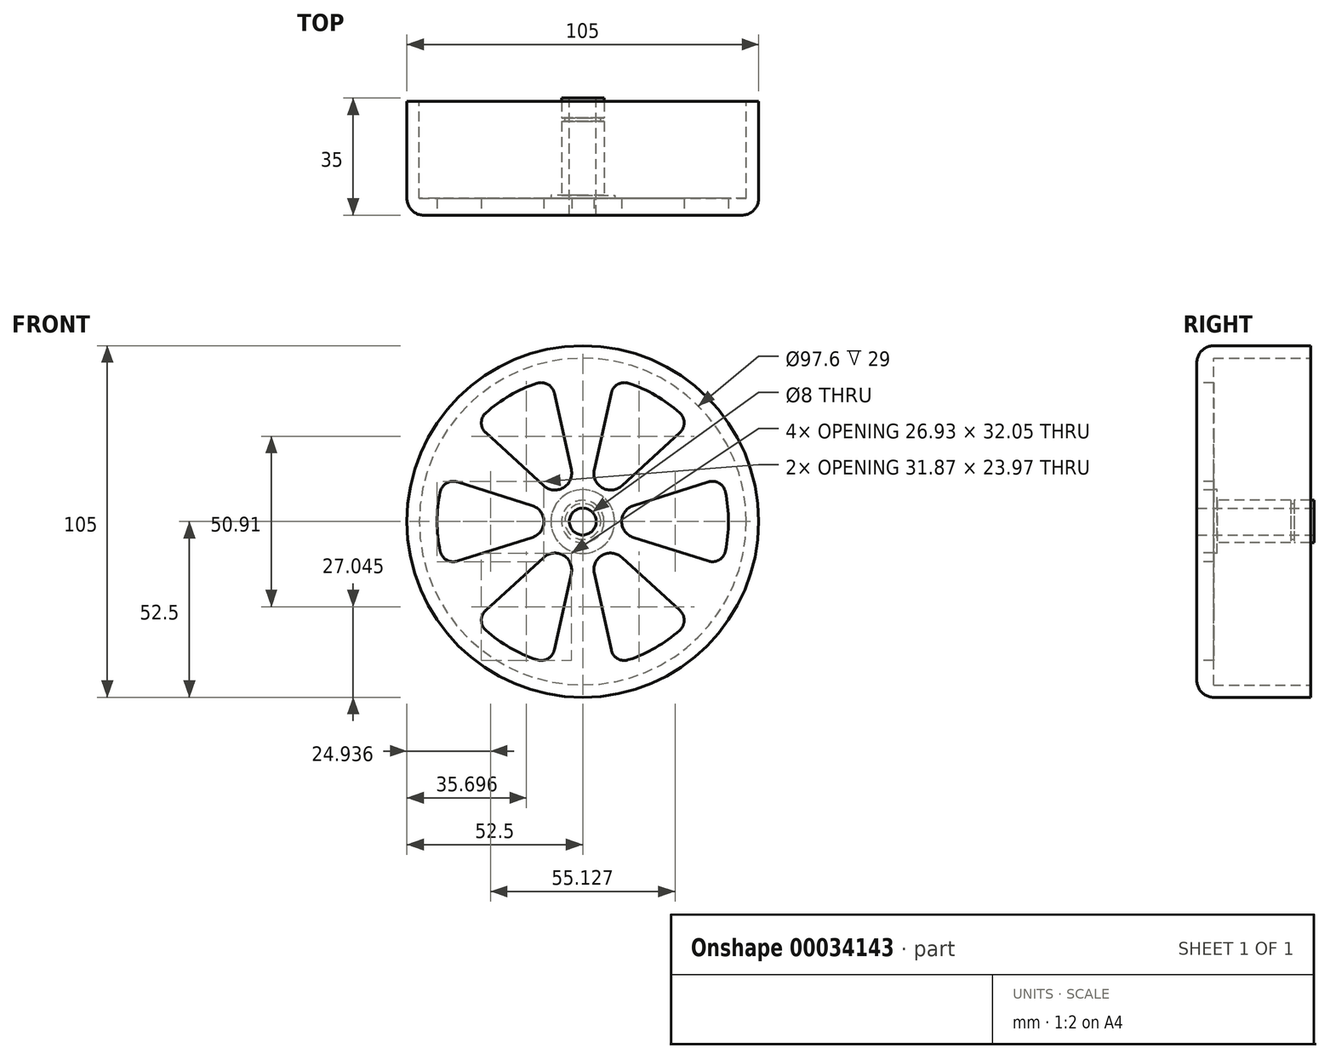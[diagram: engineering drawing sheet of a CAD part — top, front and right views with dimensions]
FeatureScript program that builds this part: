
annotation { "Feature Type Name" : "Feature", "Feature Type Description" : "" }
export const myFeature = defineFeature(function(context is Context, id is Id, definition is map)
    precondition{}
    {
        {
            var Q0;
            Q0=qCreatedBy(makeId("Front.planeOp"),FACE);
            var sketch = newSketch(context, id + "F0", { "sketchPlane" : qUnion([Q0])});
            skCircle(sketch, "E0", {"center": v(0, 0) * mm, "radius": 48.8 * mm});
            skCircle(sketch, "E1", {"center": v(0, 0) * mm, "radius": 52.5 * mm});
            skSolve(sketch);
        }
        {
            var Q0;
            Q0 = qSketchRegion(id + "F0", true);
            extrude(context, id + "F1", {"entities" : qUnion([Q0]), "depth" : 29 * mm});
        }
        {
            var Q0;
            Q0=makeQuery(id+"F1.opExtrude","CAP_FACE",FACE,{"disambiguationData":[OSD([sQuery(id+"F0.wireOp",EDGE,"E0"),sQuery(id+"F0.wireOp",EDGE,"E1")])],"isStart":false});
            var sketch = newSketch(context, id + "F2", { "sketchPlane" : qUnion([Q0])});
            skCircle(sketch, "E2.0", {"center": v(0, 0) * mm, "radius": 52.5 * mm});
            skCircle(sketch, "E3", {"center": v(0, 0) * mm, "radius": 4 * mm});
            skSolve(sketch);
        }
        {
            var Q0;
            Q0 = qSketchRegion(id + "F2", true);
            extrude(context, id + "F3", {"entities" : qUnion([Q0]), "operationType" : NewBodyOperationType.ADD, "depth" : 5 * mm});
        }
        {
            var Q0;
            Q0=makeQuery(id+"F3.opExtrude","CAP_FACE",FACE,{"disambiguationData":[OSD([sQuery(id+"F2.wireOp",EDGE,"E2.0"),sQuery(id+"F2.wireOp",EDGE,"E3")])],"isStart":true});
            var sketch = newSketch(context, id + "F4", { "sketchPlane" : qUnion([Q0])});
            skCircle(sketch, "E4", {"center": v(0, 0) * mm, "radius": 6.35 * mm});
            skCircle(sketch, "E5.0", {"center": v(0, 0) * mm, "radius": 4 * mm});
            skSolve(sketch);
        }
        {
            var Q0;
            Q0 = qSketchRegion(id + "F4", true);
            extrude(context, id + "F5", {"entities" : qUnion([Q0]), "operationType" : NewBodyOperationType.ADD, "depth" : 30 * mm});
        }
        {
            var Q0;
            Q0=makeQuery(id+"F5.opExtrude","CAP_FACE",FACE,{"disambiguationData":[OSD([sQuery(id+"F4.wireOp",EDGE,"E4"),sQuery(id+"F4.wireOp",EDGE,"E5.0")])],"isStart":false});
            cPlane(context, id + "F6", {"entities" : qUnion([Q0]), "cplaneType" : CPlaneType.OFFSET, "offset" : 6 * mm, "oppositeDirection" : true, "width" : 150 * mm, "height" : 150 * mm});
        }
        {
            var Q0;
            Q0=qCreatedBy(id+"F6.planeOp",FACE);
            var sketch = newSketch(context, id + "F7", { "sketchPlane" : qUnion([Q0])});
            skCircle(sketch, "E6", {"center": v(0, 0) * mm, "radius": 6.85 * mm});
            skCircle(sketch, "E7", {"center": v(0, 0) * mm, "radius": 5.35 * mm});
            skSolve(sketch);
        }
        {
            var Q0;
            Q0 = qSketchRegion(id + "F7", true);
            extrude(context, id + "F8", {"entities" : qUnion([Q0]), "operationType" : NewBodyOperationType.REMOVE, "oppositeDirection" : true, "depth" : 1 * mm});
        }
        {
            var Q0;
            Q0=makeQuery(id+"F3.opExtrude","CAP_FACE",FACE,{"disambiguationData":[OSD([sQuery(id+"F2.wireOp",EDGE,"E2.0"),sQuery(id+"F2.wireOp",EDGE,"E3")])],"isStart":true});
            var sketch = newSketch(context, id + "F9", { "sketchPlane" : qUnion([Q0])});
            skCircle(sketch, "E8", {"center": v(0, 0) * mm, "radius": 9.53 * mm});
            skCircle(sketch, "E9", {"center": v(0, 0) * mm, "radius": 4.38 * mm});
            skSolve(sketch);
        }
        {
            var Q0;
            Q0 = qSketchRegion(id + "F9", true);
            extrude(context, id + "F10", {"entities" : qUnion([Q0]), "operationType" : NewBodyOperationType.ADD, "depth" : 1 * mm});
        }
        {
            var Q0;
            Q0=makeQuery(id+"F3.opExtrude","CAP_EDGE",EDGE,{"disambiguationData":[OSD([sQuery(id+"F2.wireOp",EDGE,"E2.0")])],"isStart":false});
            fillet(context, id + "F11", {"entities" : qUnion([Q0]), "radius" : 5 * mm, "tangentPropagation" : true, "allowEdgeOverflow" : false});
        }
        {
            var Q0;
            Q0=makeQuery(id+"F3.opExtrude","CAP_FACE",FACE,{"disambiguationData":[OSD([sQuery(id+"F2.wireOp",EDGE,"E2.0"),sQuery(id+"F2.wireOp",EDGE,"E3")])],"isStart":false});
            var sketch = newSketch(context, id + "F12", { "sketchPlane" : qUnion([Q0])});
            skArc(sketch, "E10", {"start": v(42.6, 8.81) * mm, "mid": v(43.5, 0) * mm, "end": v(42.6, -8.81) * mm});
            skLineSegment(sketch, "E11", {"start": v(37.48, 11.82) * mm, "end": v(15.12, 4.77) * mm});
            skLineSegment(sketch, "E12", {"start": v(15.12, -4.77) * mm, "end": v(37.48, -11.82) * mm});
            skArc(sketch, "E13.filletArc", {"start": v(15.12, 4.77) * mm, "mid": v(11.63, 0) * mm, "end": v(15.12, -4.77) * mm});
            skPoint(sketch, "E14.visualSharp", {"position": v(41.49, 13.08) * mm});
            skArc(sketch, "E14.filletArc", {"start": v(42.6, 8.81) * mm, "mid": v(40.7, 11.45) * mm, "end": v(37.48, 11.82) * mm});
            skPoint(sketch, "E15.visualSharp", {"position": v(41.49, -13.08) * mm});
            skArc(sketch, "E15.filletArc", {"start": v(37.48, -11.82) * mm, "mid": v(40.7, -11.45) * mm, "end": v(42.6, -8.81) * mm});
            skArc(sketch, "E16.1.0", {"start": v(13.67, 41.3) * mm, "mid": v(21.75, 37.67) * mm, "end": v(28.93, 32.48) * mm});
            skLineSegment(sketch, "E16.1.1", {"start": v(11.7, 10.71) * mm, "end": v(28.97, 26.55) * mm});
            skPoint(sketch, "E16.1.2", {"position": v(9.42, 42.47) * mm});
            skArc(sketch, "E16.1.3", {"start": v(3.43, 15.48) * mm, "mid": v(5.81, 10.07) * mm, "end": v(11.7, 10.71) * mm});
            skLineSegment(sketch, "E16.1.4", {"start": v(8.5, 38.37) * mm, "end": v(3.43, 15.48) * mm});
            skArc(sketch, "E16.1.5", {"start": v(13.67, 41.3) * mm, "mid": v(10.44, 40.98) * mm, "end": v(8.5, 38.37) * mm});
            skArc(sketch, "E16.1.6", {"start": v(28.97, 26.55) * mm, "mid": v(30.27, 29.53) * mm, "end": v(28.93, 32.48) * mm});
            skPoint(sketch, "E16.1.7", {"position": v(32.07, 29.39) * mm});
            skArc(sketch, "E16.2.0", {"start": v(-28.93, 32.48) * mm, "mid": v(-21.75, 37.67) * mm, "end": v(-13.67, 41.3) * mm});
            skLineSegment(sketch, "E16.2.1", {"start": v(-3.43, 15.48) * mm, "end": v(-8.5, 38.37) * mm});
            skPoint(sketch, "E16.2.2", {"position": v(-32.07, 29.39) * mm});
            skArc(sketch, "E16.2.3", {"start": v(-11.7, 10.71) * mm, "mid": v(-5.81, 10.07) * mm, "end": v(-3.43, 15.48) * mm});
            skLineSegment(sketch, "E16.2.4", {"start": v(-28.97, 26.55) * mm, "end": v(-11.7, 10.71) * mm});
            skArc(sketch, "E16.2.5", {"start": v(-28.93, 32.48) * mm, "mid": v(-30.27, 29.53) * mm, "end": v(-28.97, 26.55) * mm});
            skArc(sketch, "E16.2.6", {"start": v(-8.5, 38.37) * mm, "mid": v(-10.44, 40.98) * mm, "end": v(-13.67, 41.3) * mm});
            skPoint(sketch, "E16.2.7", {"position": v(-9.42, 42.47) * mm});
            skArc(sketch, "E16.3.0", {"start": v(-42.6, -8.81) * mm, "mid": v(-43.5, 0) * mm, "end": v(-42.6, 8.81) * mm});
            skLineSegment(sketch, "E16.3.1", {"start": v(-15.12, 4.77) * mm, "end": v(-37.48, 11.82) * mm});
            skPoint(sketch, "E16.3.2", {"position": v(-41.49, -13.08) * mm});
            skArc(sketch, "E16.3.3", {"start": v(-15.12, -4.77) * mm, "mid": v(-11.63, 0) * mm, "end": v(-15.12, 4.77) * mm});
            skLineSegment(sketch, "E16.3.4", {"start": v(-37.48, -11.82) * mm, "end": v(-15.12, -4.77) * mm});
            skArc(sketch, "E16.3.5", {"start": v(-42.6, -8.81) * mm, "mid": v(-40.7, -11.45) * mm, "end": v(-37.48, -11.82) * mm});
            skArc(sketch, "E16.3.6", {"start": v(-37.48, 11.82) * mm, "mid": v(-40.7, 11.45) * mm, "end": v(-42.6, 8.81) * mm});
            skPoint(sketch, "E16.3.7", {"position": v(-41.49, 13.08) * mm});
            skArc(sketch, "E16.4.0", {"start": v(-13.67, -41.3) * mm, "mid": v(-21.75, -37.67) * mm, "end": v(-28.93, -32.48) * mm});
            skLineSegment(sketch, "E16.4.1", {"start": v(-11.7, -10.71) * mm, "end": v(-28.97, -26.55) * mm});
            skPoint(sketch, "E16.4.2", {"position": v(-9.42, -42.47) * mm});
            skArc(sketch, "E16.4.3", {"start": v(-3.43, -15.48) * mm, "mid": v(-5.81, -10.07) * mm, "end": v(-11.7, -10.71) * mm});
            skLineSegment(sketch, "E16.4.4", {"start": v(-8.5, -38.37) * mm, "end": v(-3.43, -15.48) * mm});
            skArc(sketch, "E16.4.5", {"start": v(-13.67, -41.3) * mm, "mid": v(-10.44, -40.98) * mm, "end": v(-8.5, -38.37) * mm});
            skArc(sketch, "E16.4.6", {"start": v(-28.97, -26.55) * mm, "mid": v(-30.27, -29.53) * mm, "end": v(-28.93, -32.48) * mm});
            skPoint(sketch, "E16.4.7", {"position": v(-32.07, -29.39) * mm});
            skArc(sketch, "E16.5.0", {"start": v(28.93, -32.48) * mm, "mid": v(21.75, -37.67) * mm, "end": v(13.67, -41.3) * mm});
            skLineSegment(sketch, "E16.5.1", {"start": v(3.43, -15.48) * mm, "end": v(8.5, -38.37) * mm});
            skPoint(sketch, "E16.5.2", {"position": v(32.07, -29.39) * mm});
            skArc(sketch, "E16.5.3", {"start": v(11.7, -10.71) * mm, "mid": v(5.81, -10.07) * mm, "end": v(3.43, -15.48) * mm});
            skLineSegment(sketch, "E16.5.4", {"start": v(28.97, -26.55) * mm, "end": v(11.7, -10.71) * mm});
            skArc(sketch, "E16.5.5", {"start": v(28.93, -32.48) * mm, "mid": v(30.27, -29.53) * mm, "end": v(28.97, -26.55) * mm});
            skArc(sketch, "E16.5.6", {"start": v(8.5, -38.37) * mm, "mid": v(10.44, -40.98) * mm, "end": v(13.67, -41.3) * mm});
            skPoint(sketch, "E16.5.7", {"position": v(9.42, -42.47) * mm});
            skSolve(sketch);
        }
        {
            var Q0;
            Q0 = qSketchRegion(id + "F12", true);
            extrude(context, id + "F13", {"entities" : qUnion([Q0]), "operationType" : NewBodyOperationType.REMOVE, "oppositeDirection" : true, "depth" : 25 * mm});
        }
    });
